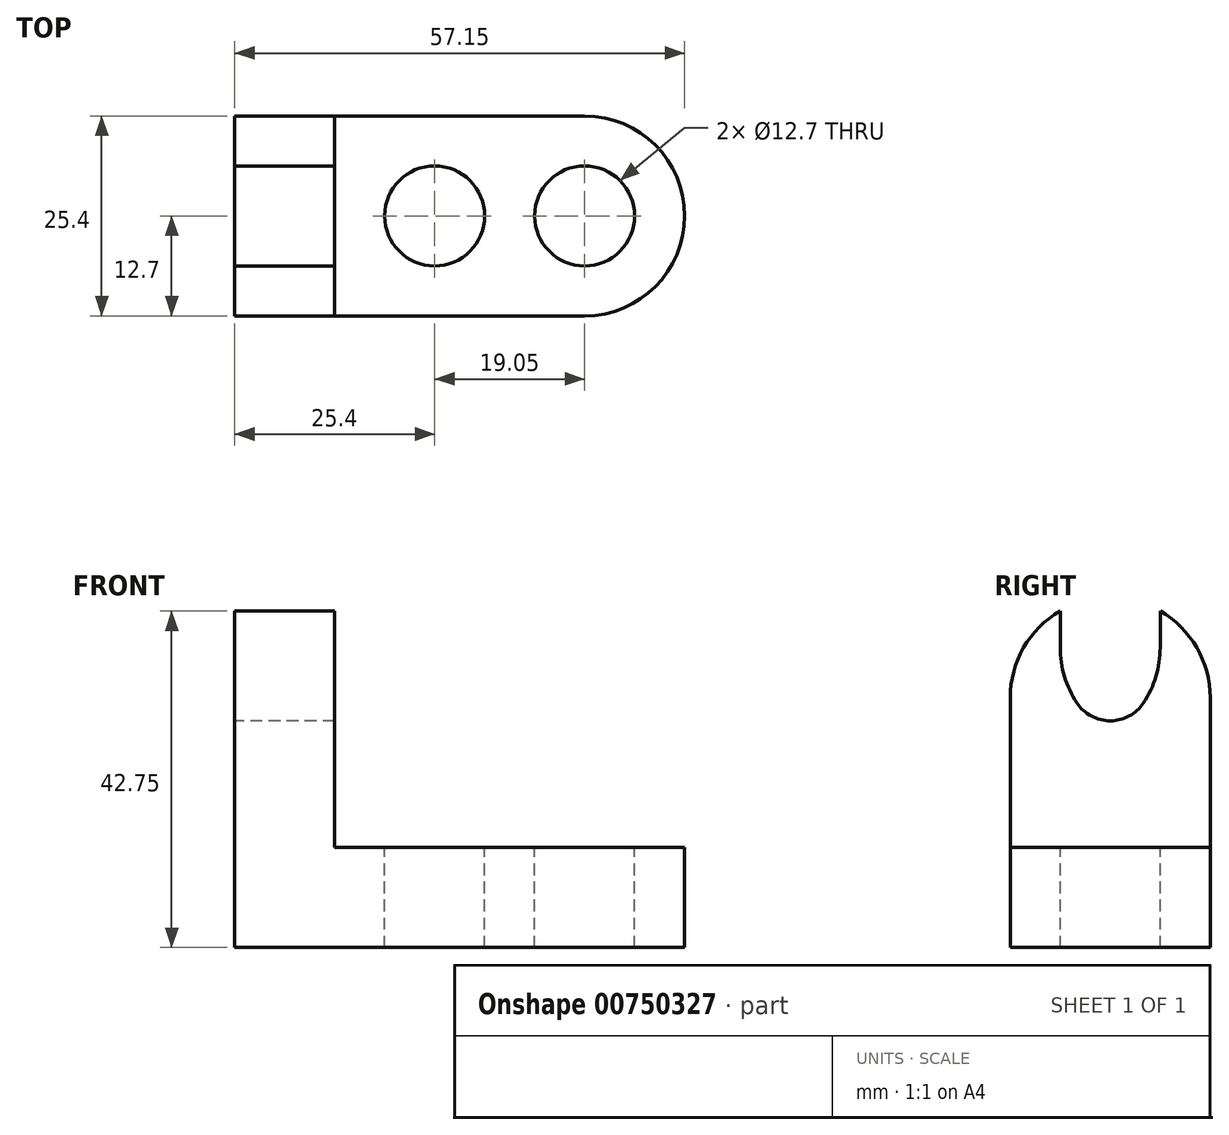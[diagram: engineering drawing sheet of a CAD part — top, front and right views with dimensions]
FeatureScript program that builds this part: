
annotation { "Feature Type Name" : "Feature", "Feature Type Description" : "" }
export const myFeature = defineFeature(function(context is Context, id is Id, definition is map)
    precondition{}
    {
        {
            var Q0;
            Q0=qCreatedBy(makeId("Front.planeOp"),FACE);
            var sketch = newSketch(context, id + "F0", { "sketchPlane" : qUnion([Q0])});
            skLineSegment(sketch, "E0", {"start": v(0, 0) * mm, "end": v(0, 44.45) * mm});
            skLineSegment(sketch, "E1", {"start": v(0, 44.45) * mm, "end": v(12.7, 44.45) * mm});
            skLineSegment(sketch, "E2", {"start": v(12.7, 44.45) * mm, "end": v(12.7, 12.7) * mm});
            skLineSegment(sketch, "E3", {"start": v(12.7, 12.7) * mm, "end": v(57.15, 12.7) * mm});
            skLineSegment(sketch, "E4", {"start": v(57.15, 12.7) * mm, "end": v(57.15, 0) * mm});
            skLineSegment(sketch, "E5", {"start": v(57.15, 0) * mm, "end": v(0, 0) * mm});
            skSolve(sketch);
        }
        {
            var Q0;
            Q0=makeQuery(id+"F0.imprint","IMPRINT",FACE,{"disambiguationData":[TD([[makeQuery(id+"F0.imprint","IMPRINT",EDGE,{"derivedFrom":sQuery(id+"F0.wireOp",EDGE,"E0")}),-1.0]])]});
            extrude(context, id + "F1", {"entities" : qUnion([Q0]), "depth" : 25.4 * mm, "offsetDistance" : 25.4 * mm});
        }
        {
            var Q0;
            Q0=makeQuery(id+"F1.opExtrude","CAP_EDGE",EDGE,{"disambiguationData":[OSD([sQuery(id+"F0.wireOp",EDGE,"E4")])],"isStart":false});
            fillet(context, id + "F2", {"entities" : qUnion([Q0]), "radius" : 12.7 * mm, "tangentPropagation" : true, "allowEdgeOverflow" : false});
        }
        {
            var Q0;
            Q0=makeQuery(id+"F1.opExtrude","CAP_EDGE",EDGE,{"disambiguationData":[OSD([sQuery(id+"F0.wireOp",EDGE,"E4")])],"isStart":true});
            fillet(context, id + "F3", {"entities" : qUnion([Q0]), "radius" : 12.7 * mm, "tangentPropagation" : true, "allowEdgeOverflow" : false});
        }
        {
            var Q0;
            Q0=makeQuery(id+"F1.opExtrude","CAP_EDGE",EDGE,{"disambiguationData":[OSD([sQuery(id+"F0.wireOp",EDGE,"E1")])],"isStart":false});
            fillet(context, id + "F4", {"entities" : qUnion([Q0]), "radius" : 12.7 * mm, "tangentPropagation" : true, "allowEdgeOverflow" : false});
        }
        {
            var Q0;
            Q0=makeQuery(id+"F1.opExtrude","CAP_EDGE",EDGE,{"disambiguationData":[OSD([sQuery(id+"F0.wireOp",EDGE,"E1")])],"isStart":true});
            fillet(context, id + "F5", {"entities" : qUnion([Q0]), "radius" : 12.7 * mm, "tangentPropagation" : true, "allowEdgeOverflow" : false});
        }
        {
            var Q0;
            Q0=makeQuery(id+"F1.opExtrude","SWEPT_FACE",FACE,{"disambiguationData":[OSD([sQuery(id+"F0.wireOp",EDGE,"E2")])]});
            var sketch = newSketch(context, id + "F6", { "sketchPlane" : qUnion([Q0])});
            skLineSegment(sketch, "E6.bottom", {"start": v(-19.05, 42.75) * mm, "end": v(-6.35, 42.75) * mm});
            skLineSegment(sketch, "E6.top", {"start": v(-19.05, 25.4) * mm, "end": v(-6.35, 25.4) * mm});
            skLineSegment(sketch, "E6.left", {"start": v(-19.05, 42.75) * mm, "end": v(-19.05, 25.4) * mm});
            skLineSegment(sketch, "E6.right", {"start": v(-6.35, 42.75) * mm, "end": v(-6.35, 25.4) * mm});
            skSolve(sketch);
        }
        {
            var Q0;
            {var subQ1=sQuery(id+"F6.wireOp",EDGE,"E6.top");Q0=makeQuery(id+"F6.imprint","IMPRINT",FACE,{"disambiguationData":[TD([[makeQuery(id+"F6.imprint","IMPRINT",EDGE,{"derivedFrom":subQ1}),1.0]])]});}
            extrude(context, id + "F7", {"entities" : qUnion([Q0]), "operationType" : NewBodyOperationType.REMOVE, "oppositeDirection" : true, "depth" : 25.4 * mm, "offsetDistance" : 25.4 * mm});
        }
        {
            var Q0;
            Q0=makeQuery(id+"F7.boolean.opBoolean","SPLIT",FACE,{"disambiguationData":[TD([makeQuery(id+"F7.opExtrude","SWEPT_FACE",FACE,{"disambiguationData":[OSD([sQuery(id+"F6.wireOp",EDGE,"E6.bottom")])]})])],"derivedFrom":makeQuery(id+"F1.opExtrude","SWEPT_FACE",FACE,{"disambiguationData":[OSD([sQuery(id+"F0.wireOp",EDGE,"E2")])]})});
            extrude(context, id + "F8", {"entities" : qUnion([Q0]), "operationType" : NewBodyOperationType.REMOVE, "oppositeDirection" : true, "depth" : 25.4 * mm, "offsetDistance" : 25.4 * mm});
        }
        {
            var Q0;
            Q0=makeQuery(id+"F7.boolean.opBoolean","COPY",EDGE,{"derivedFrom":makeQuery(id+"F7.opExtrude","SWEPT_EDGE",EDGE,{"disambiguationData":[OSD([sQuery(id+"F6.wireOp",EDGE,"E6.top"),sQuery(id+"F6.wireOp",EDGE,"E6.left")])]})});
            var Q1;
            Q1=makeQuery(id+"F7.boolean.opBoolean","COPY",EDGE,{"derivedFrom":makeQuery(id+"F7.opExtrude","SWEPT_EDGE",EDGE,{"disambiguationData":[OSD([sQuery(id+"F6.wireOp",EDGE,"E6.top"),sQuery(id+"F6.wireOp",EDGE,"E6.right")])]})});
            fillet(context, id + "F9", {"entities" : qUnion([Q0, Q1]), "radius" : 12.7 * mm, "tangentPropagation" : true, "allowEdgeOverflow" : false});
        }
        {
            var Q0;
            {var subQ0=sQuery(id+"F6.wireOp",EDGE,"E6.top");Q0=makeQuery(id+"F9.opFillet","BLEND_EDGE",EDGE,{"blendedFrom":[makeQuery(id+"F7.boolean.opBoolean","COPY",EDGE,{"derivedFrom":makeQuery(id+"F7.opExtrude","SWEPT_EDGE",EDGE,{"disambiguationData":[OSD([subQ0,sQuery(id+"F6.wireOp",EDGE,"E6.left")])]})}),makeQuery(id+"F7.boolean.opBoolean","COPY",EDGE,{"derivedFrom":makeQuery(id+"F7.opExtrude","SWEPT_EDGE",EDGE,{"disambiguationData":[OSD([subQ0,sQuery(id+"F6.wireOp",EDGE,"E6.right")])]})})],"blendedInto":[]});}
            fillet(context, id + "F10", {"entities" : qUnion([Q0]), "radius" : 5.08 * mm, "tangentPropagation" : true, "allowEdgeOverflow" : false});
        }
        {
            var Q0;
            Q0=makeQuery(id+"F1.opExtrude","SWEPT_FACE",FACE,{"disambiguationData":[OSD([sQuery(id+"F0.wireOp",EDGE,"E3")])]});
            var sketch = newSketch(context, id + "F11", { "sketchPlane" : qUnion([Q0])});
            skCircle(sketch, "E7", {"center": v(25.4, -12.7) * mm, "radius": 6.35 * mm});
            skCircle(sketch, "E8", {"center": v(44.45, -12.7) * mm, "radius": 6.35 * mm});
            skSolve(sketch);
        }
        {
            var Q0;
            Q0=makeQuery(id+"F11.imprint","IMPRINT",FACE,{"disambiguationData":[TD([[makeQuery(id+"F11.imprint","IMPRINT",EDGE,{"derivedFrom":sQuery(id+"F11.wireOp",EDGE,"E7")}),1.0]])]});
            var Q1;
            Q1=makeQuery(id+"F11.imprint","IMPRINT",FACE,{"disambiguationData":[TD([[makeQuery(id+"F11.imprint","IMPRINT",EDGE,{"derivedFrom":sQuery(id+"F11.wireOp",EDGE,"E8")}),1.0]])]});
            extrude(context, id + "F12", {"entities" : qUnion([Q0, Q1]), "operationType" : NewBodyOperationType.REMOVE, "oppositeDirection" : true, "depth" : 12.7 * mm, "offsetDistance" : 25.4 * mm});
        }
    });
